# Revit family: Sanitary_Showers_AXOR_26431CHN-AXOR-ShowerSolutions-Shower-arm222
name_source: partatom
category: Plumbing Fixtures
revit_build: Autodesk Revit 2018 (Build: 20170223_1515(x64)
units: mm (PartAtom-declared; Revit-internal decimal feet)

## family parameters
Always vertical = No
Cut with Voids When Loaded = No
OmniClass Number = 23.31.17.19
OmniClass Title = Shower Head Fixtures
Part Type = Normal
Room Calculation Point = No
Round Connector Dimension = Use Diameter
Shared = No
Work Plane-Based = Yes

## types (4) — shared parameters
Always visible = Yes
BIMobject category = Showers
Default Elevation = 1219.2 mm
Description = AXOR Shower Solutions Shower arm 390 mm
Design country = Germany
EAN code = 4059625354117
Edition number = 1
GTIN code = https://4059625354117
IFC Classification = Sanitary Terminal
Installation instructions = https://www.axor-design.com
Manufacturer = AXOR
Manufacturer country = Germany
Manufacturer name = AXOR
Model = 26431CHN
OmniClass Code = 23-31 17 19
OmniClass Description = Shower Head Fixtures
Product Guid = 026233f0-3b41-4e48-a583-0d746020d14c
Product SKU = 26431CHN
Product data url = https://www.bimobject.com
Product family = AXOR ShowerSolutions
Product group = Shower arms
Product name = 26431CHN AXOR ShowerSolutions Shower arm 390 mm
Product url = https://www.axor-design.com
QR code = https://www.bimobject.com
URL = https://www.axor-design.com
Water Inlet = 13 mm
Water Inlet Description = Water  Inlet 12.7 mm
Weight Net (Kg) = 1,5

## per-type parameters (varying)
| type | Material 1 |
| 677 Matt Black | AXOR - Metal - 677 Matt Black |
| 347 Brushed Black Chrome | AXOR - Metal - 347 Brushed Black Chrome |
| 007 Chrome | AXOR - Metal - 007 Chrome |
| 997 Polished Gold Optic | AXOR - Metal - 997 Polished Gold Optic |

## geometry (parser evidence)
native form markers: Sweep x1
no freeform markers — native parametric forms only
